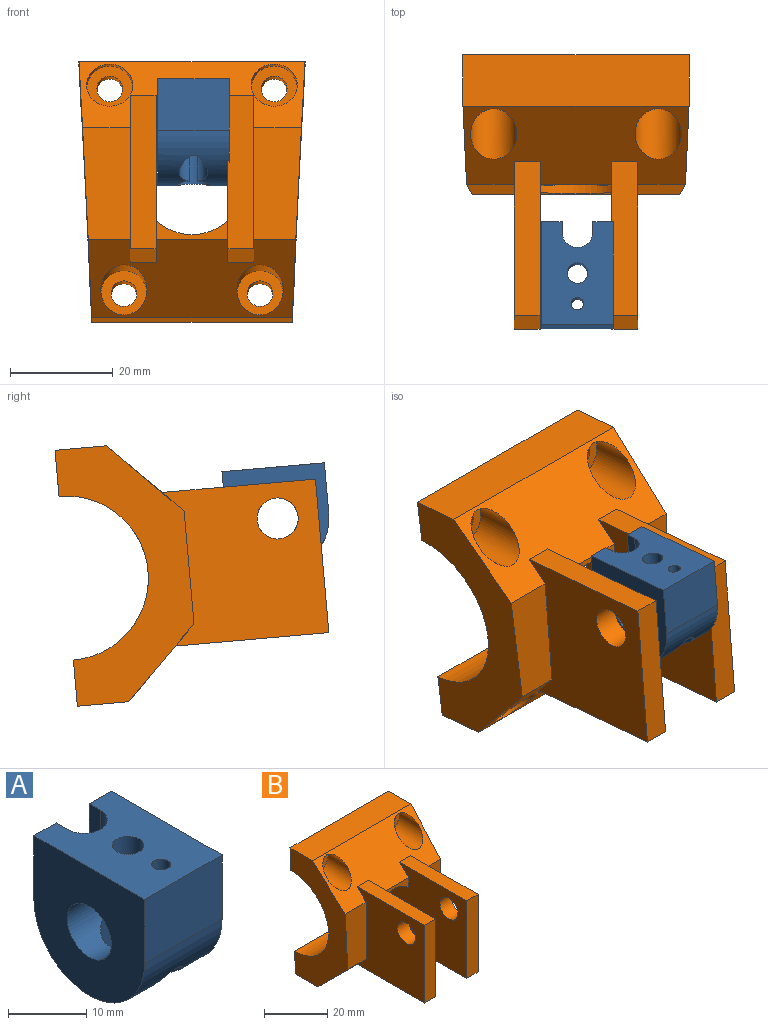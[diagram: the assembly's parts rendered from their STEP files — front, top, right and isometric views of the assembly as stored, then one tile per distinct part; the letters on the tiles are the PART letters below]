
ASSEMBLY  parts=2 mates=1
PART A: 17 faces, bbox 14x20x20 mm
  f0: plane 10x4mm, normal (0,1,0), area 40mm2, adj f1,f3,f6,f12
  f1: plane 20x14mm, normal (0,0,1), area 236.8mm2, adj f0,f2,f4,f6,f7,f8,f9,f10
  f2: plane 14x10mm, normal (0,-1,0), area 140mm2, adj f1,f3,f6,f7
  f3: cylinder r=10mm len=20mm, axis (-1,0,0), area 311.9mm2, adj f0,f2,f4,f6,f7,f10,f11,f12
  f4: plane 10x4mm, normal (0,1,0), area 40mm2, adj f1,f3,f7,f10
  f5: cylinder r=4mm len=14mm, axis (-1,0,0), area 249.8mm2, adj f6,f7,f13,f14,f15
  f6: plane 20x20mm, normal (1,0,0), area 306.8mm2, adj f0,f1,f2,f3,f5
  f7: plane 20x20mm, normal (-1,0,0), area 306.8mm2, adj f1,f2,f3,f4,f5
  f8: cylinder r=2mm len=4mm, axis (0,0,1), area 50.3mm2, adj f1,f16
  f9: cylinder r=1.2mm len=4mm, axis (0,0,1), area 30.2mm2, adj f1,f16
  f10: plane 16x2mm, normal (1,0,0), area 28.2mm2, adj f1,f3,f4,f11
  f11: cylinder r=3mm len=18.66mm, axis (0,0,1), area 168.1mm2, adj f1,f3,f10,f12
  f12: plane 16x2mm, normal (-1,0,0), area 28.2mm2, adj f0,f1,f3,f11
  f13: cylinder r=3.5mm len=8.06mm, axis (0,0,1), area 132.8mm2, adj f3,f5,f15
  f14: cylinder r=3.5mm len=7mm, axis (0,0,1), area 57.7mm2, adj f5,f15,f16
  f15: cylinder r=2.75mm len=15.41mm, axis (0,0,1), area 200.2mm2, adj f3,f5,f13,f14,f16
  f16: plane 12.25x7mm, normal (0,0,-1), area 44.9mm2, adj f8,f9,f14,f15
PART B: 39 faces, bbox 44x50x50 mm
  f0: plane 14x3.86mm, normal (0,-1,0), area 26.5mm2, adj f4,f26,f31,f35
  f1: plane 22x9.3mm, normal (0,-1,0), area 192.5mm2, adj f3,f4,f6,f32
  f2: plane 14x3.86mm, normal (0,-1,0), area 26.5mm2, adj f3,f26,f31,f36
  f3: plane 40.4x14mm, normal (0,-0.71,-0.71), area 549.5mm2, adj f1,f2,f5,f6,f7,f16,f20,f22
  f4: plane 44x14mm, normal (0,-0.71,0.71), area 620.8mm2, adj f0,f1,f5,f6,f7,f9,f10,f15
  f5: plane 50x24mm, normal (1,0,-0.05), area 602.6mm2, adj f3,f4,f7,f8,f15,f16,f17,f24
  f6: plane 50x24mm, normal (-1,0,-0.05), area 602.6mm2, adj f1,f3,f4,f8,f15,f16,f17,f24
  f7: plane 22x9.3mm, normal (0,-1,0), area 192.5mm2, adj f3,f4,f5,f27
  f8: plane 44x9mm, normal (0,1,0), area 352.7mm2, adj f5,f6,f11,f14,f15,f24
  f9: cylinder r=4.5mm len=13.06mm, axis (0,1,0), area 240.3mm2, adj f4,f18
  f10: cylinder r=4.5mm len=13.06mm, axis (0,1,0), area 240.3mm2, adj f4,f19
  f11: cylinder r=2.5mm len=6.5mm, axis (0,1,0), area 102.1mm2, adj f8,f18
  f12: cylinder r=2.5mm len=6.5mm, axis (0,1,0), area 102.1mm2, adj f17,f23
  f13: cylinder r=2.5mm len=6.5mm, axis (0,1,0), area 102.1mm2, adj f17,f21
  f14: cylinder r=2.5mm len=6.5mm, axis (0,1,0), area 102.1mm2, adj f8,f19
  f15: plane 44x10mm, normal (0,0,1), area 440mm2, adj f4,f5,f6,f8
  f16: plane 39x10mm, normal (0,0,-1), area 390mm2, adj f3,f5,f6,f17
  f17: plane 39.9x9mm, normal (0,1,0), area 315.8mm2, adj f5,f6,f12,f13,f16,f24
  f18: plane 9x9mm, normal (0,-1,0), area 44mm2, adj f9,f11
  f19: plane 9x9mm, normal (0,-1,0), area 44mm2, adj f10,f14
  f20: cylinder r=4.5mm len=13.06mm, axis (0,1,0), area 240.3mm2, adj f3,f21
  f21: plane 9x9mm, normal (0,-1,0), area 44mm2, adj f13,f20
  f22: cylinder r=4.5mm len=13.06mm, axis (0,1,0), area 240.3mm2, adj f3,f23
  f23: plane 9x9mm, normal (0,-1,0), area 44mm2, adj f12,f22
  f24: cylinder r=16mm len=43.1mm, axis (1,0,0), area 1814.1mm2, adj f5,f6,f8,f17,f26,f31,f35,f36
  f25: plane 30x5mm, normal (0,0,-1), area 150mm2, adj f3,f26,f27,f29
  f26: plane 35.68x30mm, normal (-1,0,0), area 867.8mm2, adj f0,f2,f3,f4,f24,f25,f28,f29
  f27: plane 30x30mm, normal (1,0,0), area 745.7mm2, adj f3,f4,f7,f25,f28,f29,f38
  f28: plane 30x5mm, normal (0,0,1), area 150mm2, adj f4,f26,f27,f29
  f29: plane 30x5mm, normal (0,-1,0), area 150mm2, adj f25,f26,f27,f28
  f30: plane 30x5mm, normal (0,0,-1), area 150mm2, adj f3,f31,f32,f34
  f31: plane 35.68x30mm, normal (1,0,0), area 867.8mm2, adj f0,f2,f3,f4,f24,f30,f33,f34
  f32: plane 30x30mm, normal (-1,0,0), area 745.7mm2, adj f1,f3,f4,f30,f33,f34,f37
  f33: plane 30x5mm, normal (0,0,1), area 150mm2, adj f4,f31,f32,f34
  f34: plane 30x5mm, normal (0,-1,0), area 150mm2, adj f30,f31,f32,f33
  f35: cylinder r=10mm len=14mm, axis (0,1,0), area 168mm2, adj f0,f24,f26,f31
  f36: cylinder r=10mm len=14mm, axis (0,1,0), area 168mm2, adj f2,f24,f26,f31
  f37: cylinder r=4mm len=8mm, axis (1,0,0), area 125.7mm2, adj f31,f32
  f38: cylinder r=4mm len=8mm, axis (1,0,0), area 125.7mm2, adj f26,f27
PLACE A rot(axis=(-1,0,0),5deg) t=(-0.45,0.8,0.6)mm
PLACE B rot(axis=(-1,0,0),5deg) t=(-0.74,41.95,-11.03)mm
MATE cylindrical B.f37 <-> A.f5  axis (-1,0,0) through (6.26,0.8,0.6)mm
